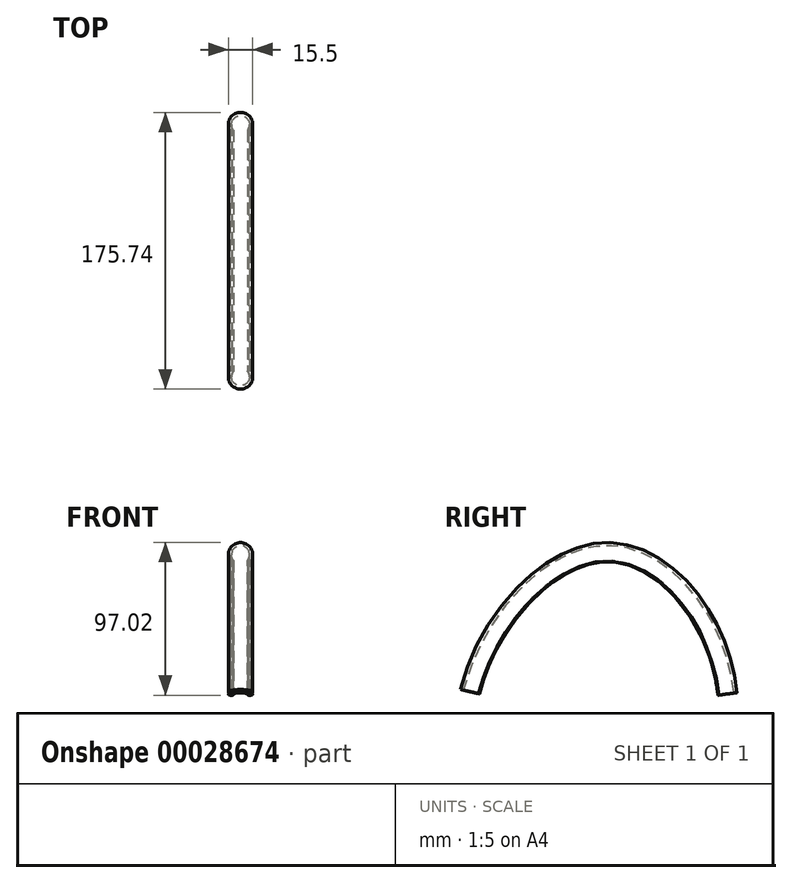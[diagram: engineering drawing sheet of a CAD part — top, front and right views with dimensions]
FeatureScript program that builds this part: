
annotation { "Feature Type Name" : "Feature", "Feature Type Description" : "" }
export const myFeature = defineFeature(function(context is Context, id is Id, definition is map)
    precondition{}
    {
        {
            var Q0;
            Q0=qCreatedBy(makeId("Front.planeOp"),FACE);
            var sketch = newSketch(context, id + "F0", { "sketchPlane" : qUnion([Q0])});
            skArc(sketch, "E0", {"start": v(4.4, 25) * mm, "mid": v(0, 34.44) * mm, "end": v(-4.4, 25) * mm});
            skArc(sketch, "E1", {"start": v(5.94, 23.7) * mm, "mid": v(0, 36.44) * mm, "end": v(-5.94, 23.7) * mm});
            skLineSegment(sketch, "E2", {"start": v(-4.4, 25) * mm, "end": v(-5.94, 23.7) * mm});
            skLineSegment(sketch, "E3", {"start": v(-5.94, 23.7) * mm, "end": v(-4.4, 25) * mm});
            skLineSegment(sketch, "E4", {"start": v(4.4, 25) * mm, "end": v(5.98, 23.68) * mm});
            skSolve(sketch);
        }
        {
            var Q0;
            Q0=qCreatedBy(makeId("Right.planeOp"),FACE);
            var sketch = newSketch(context, id + "F1", { "sketchPlane" : qUnion([Q0])});
            skFitSpline(sketch, "E5", {"points": [v(-88.1, -58.42) * mm, v(0, 29.62) * mm, v(74.22, -59.84) * mm], "startDerivative": vector(70.43, 274.57) * mm, "endDerivative": vector(29.66, -285.46) * mm});
            skSolve(sketch);
        }
        {
            var Q0;
            {var subQ0=sQuery(id+"F0.wireOp",EDGE,"E0");Q0=makeQuery(id+"F0.imprint","IMPRINT",FACE,{"disambiguationData":[TD([[makeQuery(id+"F0.imprint","IMPRINT",EDGE,{"derivedFrom":subQ0}),-1.0]])]});}
            var Q1;
            Q1=sQuery(id+"F1.wireOp",EDGE,"E5");
            sweep(context, id + "F2", {"profiles" : qUnion([Q0]), "path" : qUnion([Q1])});
        }
        {
            var Q0;
            Q0=makeQuery(id+"F2.opSweep","SWEPT_EDGE",EDGE,{"disambiguationData":[OSD([sQuery(id+"F0.wireOp",EDGE,"E1"),sQuery(id+"F0.wireOp",EDGE,"E4"),sQuery(id+"F1.wireOp",EDGE,"asFcmciT-qu6X-Ssgh-Iukl-KvLUw1eoQ70a")])]});
            var Q1;
            Q1=makeQuery(id+"F2.opSweep","SWEPT_EDGE",EDGE,{"disambiguationData":[OSD([sQuery(id+"F0.wireOp",EDGE,"E1"),sQuery(id+"F0.wireOp",EDGE,"E2"),sQuery(id+"F1.wireOp",EDGE,"asFcmciT-qu6X-Ssgh-Iukl-KvLUw1eoQ70a")])]});
            fillet(context, id + "F3", {"entities" : qUnion([Q0, Q1]), "tangentPropagation" : true, "radius" : 1 * mm, "defaultsChanged" : true, "vertexSettings" : [], "allowEdgeOverflow" : false});
        }
        {
            var Q0;
            Q0=makeQuery(id+"F2.opSweep","CAP_EDGE",EDGE,{"disambiguationData":[OSD([sQuery(id+"F0.wireOp",EDGE,"E0"),sQuery(id+"F1.wireOp",VERTEX,"E5.start")])],"isStart":false});
            var Q1;
            Q1=makeQuery(id+"F2.opSweep","CAP_EDGE",EDGE,{"disambiguationData":[OSD([sQuery(id+"F0.wireOp",EDGE,"E0"),sQuery(id+"F1.wireOp",VERTEX,"E5.end")])],"isStart":true});
            fillet(context, id + "F4", {"entities" : qUnion([Q0, Q1]), "tangentPropagation" : true, "radius" : 0.5 * mm, "defaultsChanged" : true, "vertexSettings" : [], "allowEdgeOverflow" : false});
        }
    });
